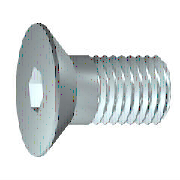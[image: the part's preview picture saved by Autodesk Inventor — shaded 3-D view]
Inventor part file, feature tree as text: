
AUTODESK INVENTOR PART (.ipt)
format: ipt  version: 2020 (Build 240168000, 168)  size: 187,904 bytes
history: native  units: mm (DEFAULTED — no unit token found)
features: other x4, sketch x3, fillet x1, chamfer x1
ambient origin geometry x8: Origin, YZ Plane, XZ Plane, XY Plane, X Axis, Y Axis, Z Axis, Center Point
bodies: Solid1 (feature_tree)
feature tree (9):
  sketch  "Sketch1"  dims[d2=3.0mm]
  other  "WorkPoint1"
  sketch  "Sketch2"  dims[d3=4.0mm]
  fillet  "Fillet1"  [1 undecoded]
  chamfer  "Chamfer1"  Distance=2.0mm
  other  "MSC_A1"
  other  "MSC_PF1"
  other  "MSC_PT1"
  sketch  "Sketch3"  dims[d4=1.5mm d5=2.0mm d6=8.0mm d7=25.0mm d8=360.0deg d9=0.0mm d10=2.0mm d11=2.5mm d12=120.0deg d13=120.0deg d14=120.0deg d15=120.0deg d16=1.8mm d17=0.0mm d18=0.2mm d19=0.35mm d20=45.0deg d22=0.0mm d23=0.0mm d35=0.0mm d37=0.0mm d38=0.0mm d39=0.35mm d40=0.0mm d41=0.0mm d42=0.0mm d43=45.0deg]
note: 1 required parameter value undecoded (feature->parameter linkage not recoverable at this tier; creation-order binding heuristic only, values carry confidence <= 0.55)
